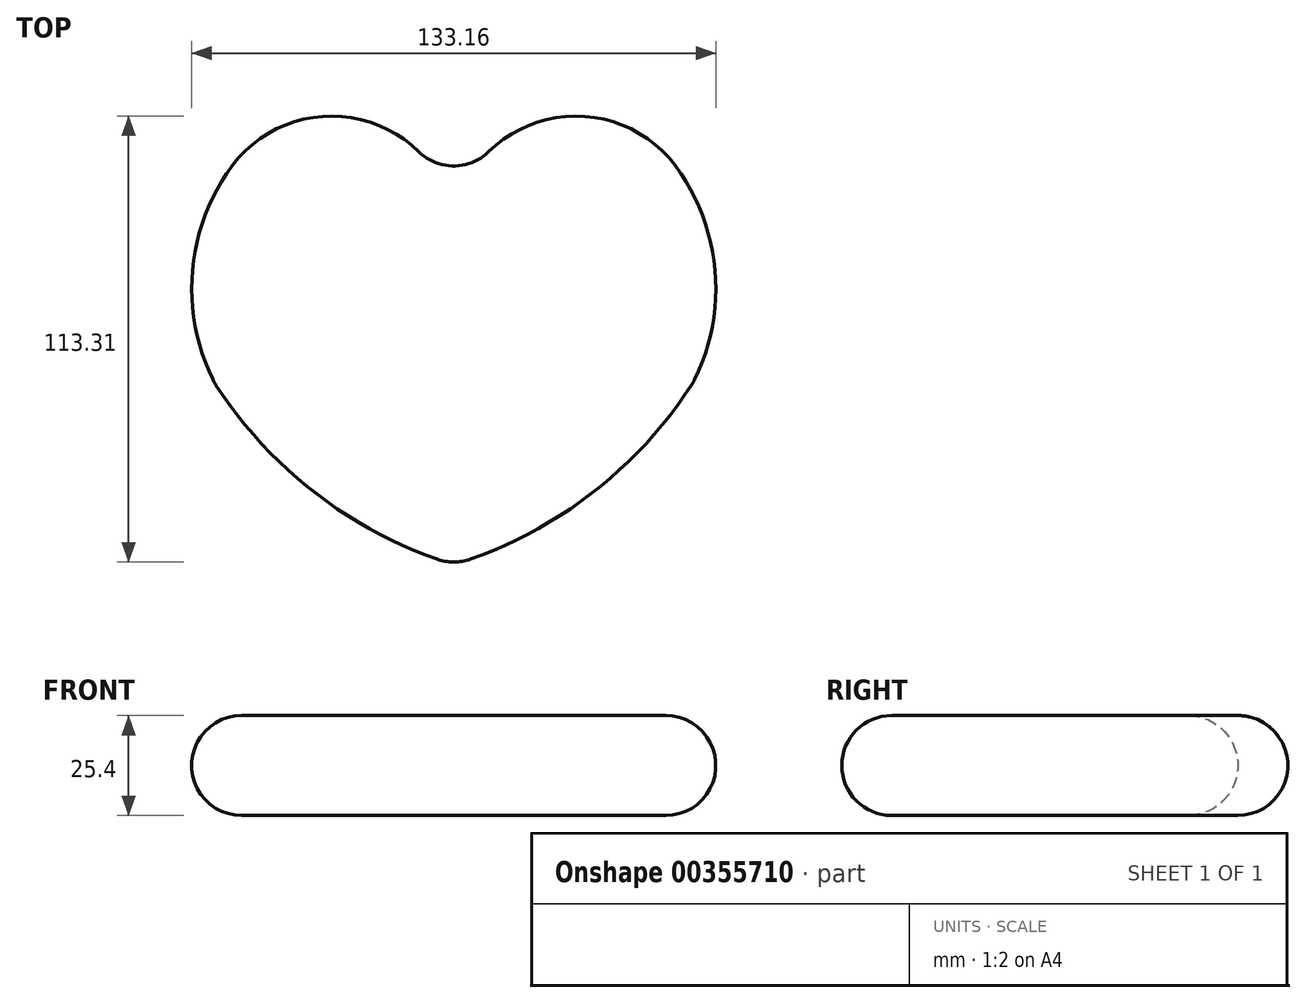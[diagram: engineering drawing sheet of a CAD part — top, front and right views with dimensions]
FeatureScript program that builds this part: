
annotation { "Feature Type Name" : "Feature", "Feature Type Description" : "" }
export const myFeature = defineFeature(function(context is Context, id is Id, definition is map)
    precondition{}
    {
        {
            var Q0;
            Q0=qCreatedBy(makeId("Top.planeOp"),FACE);
            var sketch = newSketch(context, id + "F0", { "sketchPlane" : qUnion([Q0])});
            skPoint(sketch, "E0", {"position": v(0, -77.33) * mm});
            skPoint(sketch, "E1", {"position": v(0, 0) * mm});
            skArc(sketch, "E2", {"start": v(-60.83, -31.05) * mm, "mid": v(-34.53, -59.6) * mm, "end": v(0, -77.33) * mm});
            skArc(sketch, "E3", {"start": v(-57.63, 22.13) * mm, "mid": v(-66.48, -4.02) * mm, "end": v(-60.83, -31.05) * mm});
            skArc(sketch, "E4", {"start": v(0.34, 8.95) * mm, "mid": v(-24.03, 35.86) * mm, "end": v(-57.63, 22.13) * mm});
            skArc(sketch, "E5.MirrorCS", {"start": v(57.63, 22.13) * mm, "mid": v(66.48, -4.02) * mm, "end": v(60.83, -31.05) * mm});
            skArc(sketch, "E6.MirrorCS", {"start": v(-0.34, 8.95) * mm, "mid": v(24.03, 35.86) * mm, "end": v(57.63, 22.13) * mm});
            skArc(sketch, "E7.MirrorCS", {"start": v(60.83, -31.05) * mm, "mid": v(34.53, -59.6) * mm, "end": v(0, -77.33) * mm});
            skSolve(sketch);
        }
        {
            var Q0;
            Q0=makeQuery(id+"F0.imprint","IMPRINT",FACE,{"disambiguationData":[TD([[makeQuery(id+"F0.imprint","IMPRINT",EDGE,{"derivedFrom":sQuery(id+"F0.wireOp",EDGE,"E2")}),1.0]])]});
            extrude(context, id + "F1", {"entities" : qUnion([Q0]), "depth" : 25.4 * mm});
        }
        {
            var Q0;
            Q0=makeQuery(id+"F1.opExtrude","CAP_EDGE",EDGE,{"disambiguationData":[OSD([sQuery(id+"F0.wireOp",EDGE,"E2")])],"isStart":true});
            var Q1;
            Q1=makeQuery(id+"F1.opExtrude","SWEPT_FACE",FACE,{"disambiguationData":[OSD([sQuery(id+"F0.wireOp",EDGE,"E3")])]});
            var Q2;
            Q2=makeQuery(id+"F1.opExtrude","SWEPT_FACE",FACE,{"disambiguationData":[OSD([sQuery(id+"F0.wireOp",EDGE,"E5.MirrorCS")])]});
            var Q3;
            Q3=makeQuery(id+"F1.opExtrude","CAP_EDGE",EDGE,{"disambiguationData":[OSD([sQuery(id+"F0.wireOp",EDGE,"E3")])],"isStart":true});
            var Q4;
            Q4=makeQuery(id+"F1.opExtrude","SWEPT_FACE",FACE,{"disambiguationData":[OSD([sQuery(id+"F0.wireOp",EDGE,"E4")])]});
            var Q5;
            Q5=makeQuery(id+"F1.opExtrude","CAP_FACE",FACE,{"disambiguationData":[OSD([sQuery(id+"F0.wireOp",EDGE,"E2"),sQuery(id+"F0.wireOp",EDGE,"E3"),sQuery(id+"F0.wireOp",EDGE,"E4"),sQuery(id+"F0.wireOp",EDGE,"E5.MirrorCS"),sQuery(id+"F0.wireOp",EDGE,"E6.MirrorCS"),sQuery(id+"F0.wireOp",EDGE,"E7.MirrorCS")])],"isStart":false});
            var Q6;
            Q6=makeQuery(id+"F1.opExtrude","SWEPT_FACE",FACE,{"disambiguationData":[OSD([sQuery(id+"F0.wireOp",EDGE,"E7.MirrorCS")])]});
            var Q7;
            Q7=makeQuery(id+"F1.opExtrude","CAP_FACE",FACE,{"disambiguationData":[OSD([sQuery(id+"F0.wireOp",EDGE,"E2"),sQuery(id+"F0.wireOp",EDGE,"E3"),sQuery(id+"F0.wireOp",EDGE,"E4"),sQuery(id+"F0.wireOp",EDGE,"E5.MirrorCS"),sQuery(id+"F0.wireOp",EDGE,"E6.MirrorCS"),sQuery(id+"F0.wireOp",EDGE,"E7.MirrorCS")])],"isStart":true});
            var Q8;
            Q8=makeQuery(id+"F1.opExtrude","SWEPT_FACE",FACE,{"disambiguationData":[OSD([sQuery(id+"F0.wireOp",EDGE,"E2")])]});
            var Q9;
            Q9=makeQuery(id+"F1.opExtrude","CAP_EDGE",EDGE,{"disambiguationData":[OSD([sQuery(id+"F0.wireOp",EDGE,"E6.MirrorCS")])],"isStart":false});
            var Q10;
            Q10=makeQuery(id+"F1.opExtrude","CAP_EDGE",EDGE,{"disambiguationData":[OSD([sQuery(id+"F0.wireOp",EDGE,"E6.MirrorCS")])],"isStart":true});
            var Q11;
            Q11=makeQuery(id+"F1.opExtrude","CAP_EDGE",EDGE,{"disambiguationData":[OSD([sQuery(id+"F0.wireOp",EDGE,"E5.MirrorCS")])],"isStart":false});
            var Q12;
            Q12=makeQuery(id+"F1.opExtrude","SWEPT_FACE",FACE,{"disambiguationData":[OSD([sQuery(id+"F0.wireOp",EDGE,"E6.MirrorCS")])]});
            var Q13;
            Q13=makeQuery(id+"F1.opExtrude","CAP_EDGE",EDGE,{"disambiguationData":[OSD([sQuery(id+"F0.wireOp",EDGE,"E4")])],"isStart":true});
            var Q14;
            Q14=makeQuery(id+"F1.opExtrude","CAP_EDGE",EDGE,{"disambiguationData":[OSD([sQuery(id+"F0.wireOp",EDGE,"E4")])],"isStart":false});
            var Q15;
            Q15=makeQuery(id+"F1.opExtrude","CAP_EDGE",EDGE,{"disambiguationData":[OSD([sQuery(id+"F0.wireOp",EDGE,"E5.MirrorCS")])],"isStart":true});
            var Q16;
            Q16=makeQuery(id+"F1.opExtrude","CAP_EDGE",EDGE,{"disambiguationData":[OSD([sQuery(id+"F0.wireOp",EDGE,"E7.MirrorCS")])],"isStart":true});
            var Q17;
            Q17=makeQuery(id+"F1.opExtrude","SWEPT_EDGE",EDGE,{"disambiguationData":[OSD([sQuery(id+"F0.wireOp",EDGE,"E3"),sQuery(id+"F0.wireOp",EDGE,"E4")])]});
            var Q18;
            Q18=makeQuery(id+"F1.opExtrude","SWEPT_EDGE",EDGE,{"disambiguationData":[OSD([sQuery(id+"F0.wireOp",EDGE,"E5.MirrorCS"),sQuery(id+"F0.wireOp",EDGE,"E6.MirrorCS")])]});
            var Q19;
            Q19=makeQuery(id+"F1.opExtrude","SWEPT_EDGE",EDGE,{"disambiguationData":[OSD([sQuery(id+"F0.wireOp",EDGE,"E4"),sQuery(id+"F0.wireOp",EDGE,"E6.MirrorCS")])]});
            var Q20;
            Q20=makeQuery(id+"F1.opExtrude","SWEPT_EDGE",EDGE,{"disambiguationData":[OSD([sQuery(id+"F0.wireOp",EDGE,"E5.MirrorCS"),sQuery(id+"F0.wireOp",EDGE,"E7.MirrorCS")])]});
            var Q21;
            Q21=makeQuery(id+"F1.opExtrude","SWEPT_EDGE",EDGE,{"disambiguationData":[OSD([sQuery(id+"F0.wireOp",EDGE,"E2"),sQuery(id+"F0.wireOp",EDGE,"E7.MirrorCS")])]});
            var Q22;
            Q22=makeQuery(id+"F1.opExtrude","SWEPT_EDGE",EDGE,{"disambiguationData":[OSD([sQuery(id+"F0.wireOp",EDGE,"E2"),sQuery(id+"F0.wireOp",EDGE,"E3")])]});
            var Q23;
            Q23=makeQuery(id+"F1.opExtrude","CAP_EDGE",EDGE,{"disambiguationData":[OSD([sQuery(id+"F0.wireOp",EDGE,"E2")])],"isStart":false});
            var Q24;
            Q24=makeQuery(id+"F1.opExtrude","CAP_EDGE",EDGE,{"disambiguationData":[OSD([sQuery(id+"F0.wireOp",EDGE,"E3")])],"isStart":false});
            var Q25;
            Q25=makeQuery(id+"F1.opExtrude","CAP_EDGE",EDGE,{"disambiguationData":[OSD([sQuery(id+"F0.wireOp",EDGE,"E7.MirrorCS")])],"isStart":false});
            fillet(context, id + "F2", {"entities" : qUnion([Q0, Q1, Q2, Q3, Q4, Q5, Q6, Q7, Q8, Q9, Q10, Q11, Q12, Q13, Q14, Q15, Q16, Q17, Q18, Q19, Q20, Q21, Q22, Q23, Q24, Q25]), "radius" : 12.7 * mm, "allowEdgeOverflow" : false});
        }
    });
